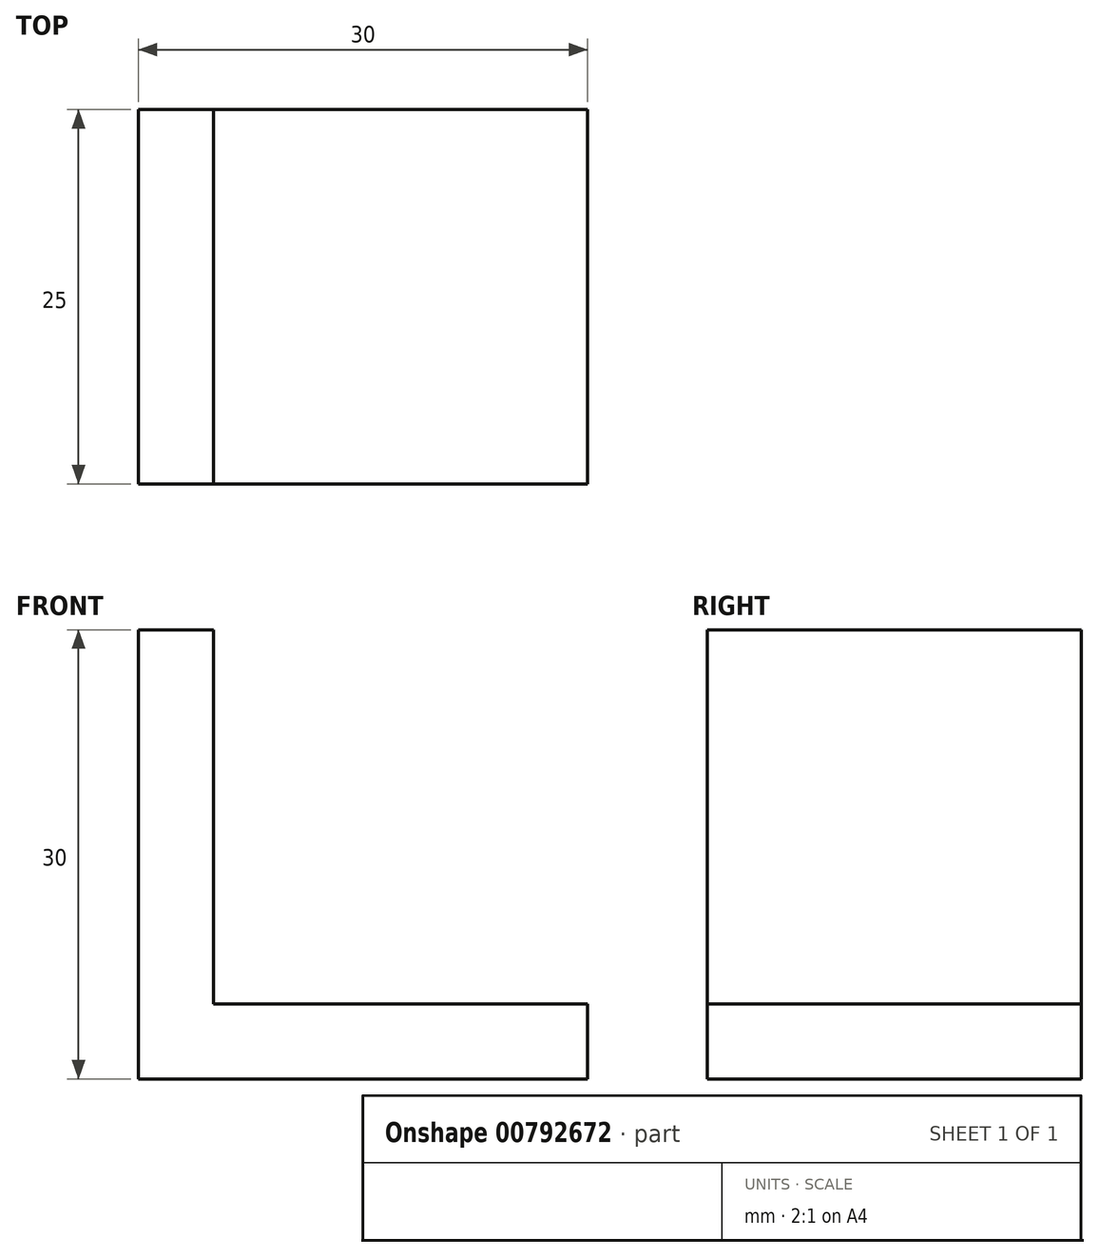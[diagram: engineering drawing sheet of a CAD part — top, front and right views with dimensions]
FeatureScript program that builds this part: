
annotation { "Feature Type Name" : "Feature", "Feature Type Description" : "" }
export const myFeature = defineFeature(function(context is Context, id is Id, definition is map)
    precondition{}
    {
        {
            var Q0;
            Q0=qCreatedBy(makeId("Front.planeOp"),FACE);
            var sketch = newSketch(context, id + "F0", { "sketchPlane" : qUnion([Q0])});
            skLineSegment(sketch, "E0", {"start": v(0, 0) * mm, "end": v(0, 30) * mm});
            skLineSegment(sketch, "E1", {"start": v(0, 30) * mm, "end": v(5, 30) * mm});
            skLineSegment(sketch, "E2", {"start": v(5, 30) * mm, "end": v(5, 5) * mm});
            skLineSegment(sketch, "E3", {"start": v(5, 5) * mm, "end": v(30, 5) * mm});
            skLineSegment(sketch, "E4", {"start": v(30, 5) * mm, "end": v(30, 0) * mm});
            skLineSegment(sketch, "E5", {"start": v(30, 0) * mm, "end": v(0, 0) * mm});
            skSolve(sketch);
        }
        {
            var Q0;
            Q0 = qSketchRegion(id + "F0", true);
            var Q1;
            Q1=makeQuery(id+"F0.imprint","IMPRINT",FACE,{"disambiguationData":[TD([[makeQuery(id+"F0.imprint","IMPRINT",EDGE,{"derivedFrom":sQuery(id+"F0.wireOp",EDGE,"E0")}),-1.0]])]});
            extrude(context, id + "F1", {"entities" : qUnion([Q0, Q1]), "depth" : 25 * mm, "offsetDistance" : 25 * mm});
        }
    });
